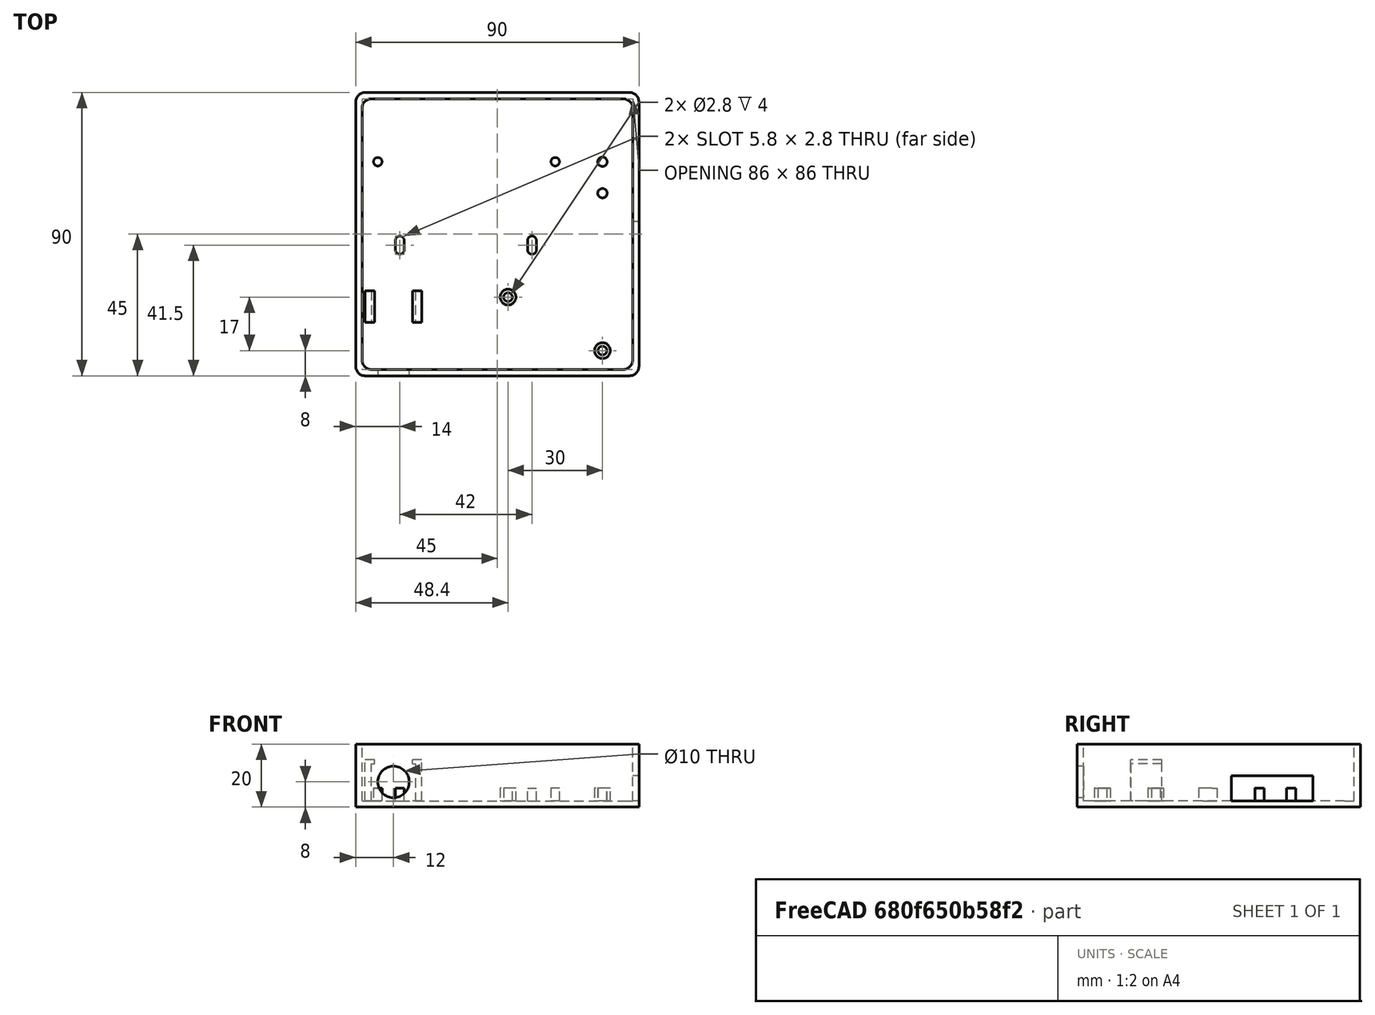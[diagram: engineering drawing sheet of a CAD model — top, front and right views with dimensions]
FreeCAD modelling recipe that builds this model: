
FCSTD DOCUMENT  (FreeCAD 1.0R39109 (Git))
Label: PowerBox
License: All rights reserved
objects: Sketcher::SketchObject×7, PartDesign::Pad×4, PartDesign::Pocket×4, PartDesign::Body×1, Mesh::Feature×1
note: 39 computed .brp shape members not serialized (recipe doc carries the construction recipe); baked Part::Feature solids carry a one-line shape summary decoded from their .brp

FEATURE [Sketcher::SketchObject] Sketch
  ArcFitTolerance = 1e-06
  AttachmentSupport = -> [XY_Plane]
  FullyConstrained = true
  MakeInternals = false
  MapMode = 5
  sketch-geometry (20):
    g0: LineSegment StartX=3 StartY=0 StartZ=0 EndX=87 EndY=0 EndZ=0
    g1: LineSegment StartX=90 StartY=3 StartZ=0 EndX=90 EndY=87 EndZ=0
    g2: LineSegment StartX=87 StartY=90 StartZ=0 EndX=3 EndY=90 EndZ=0
    g3: LineSegment StartX=0 StartY=87 StartZ=0 EndX=0 EndY=3 EndZ=0
    g4: ArcOfCircle CenterX=3 CenterY=3 CenterZ=0 NormalX=0 NormalY=0 NormalZ=1 AngleXU=0 Radius=3 StartAngle=3.14159 EndAngle=4.71239
    g5: ArcOfCircle CenterX=87 CenterY=3 CenterZ=0 NormalX=0 NormalY=0 NormalZ=1 AngleXU=0 Radius=3 StartAngle=4.71239 EndAngle=6.28319
    g6: ArcOfCircle CenterX=87 CenterY=87 CenterZ=0 NormalX=0 NormalY=0 NormalZ=1 AngleXU=0 Radius=3 StartAngle=1.1e-15 EndAngle=1.5708
    g7: ArcOfCircle CenterX=3 CenterY=87 CenterZ=0 NormalX=0 NormalY=0 NormalZ=1 AngleXU=0 Radius=3 StartAngle=1.5708 EndAngle=3.14159
    g8: GeomPoint [constr] X=0 Y=0 Z=0
    g9: GeomPoint [constr] X=90 Y=90 Z=0
    g10: LineSegment StartX=2 StartY=85 StartZ=0 EndX=2 EndY=5 EndZ=0
    g11: LineSegment StartX=5 StartY=2 StartZ=0 EndX=85 EndY=2 EndZ=0
    g12: LineSegment StartX=88 StartY=5 StartZ=0 EndX=88 EndY=85 EndZ=0
    g13: LineSegment StartX=85 StartY=88 StartZ=0 EndX=5 EndY=88 EndZ=0
    g14: ArcOfCircle CenterX=5 CenterY=85 CenterZ=0 NormalX=0 NormalY=0 NormalZ=1 AngleXU=0 Radius=3 StartAngle=1.5708 EndAngle=3.14159
    g15: ArcOfCircle CenterX=5 CenterY=5 CenterZ=0 NormalX=0 NormalY=0 NormalZ=1 AngleXU=0 Radius=3 StartAngle=3.14159 EndAngle=4.71239
    g16: ArcOfCircle CenterX=85 CenterY=5 CenterZ=0 NormalX=0 NormalY=0 NormalZ=1 AngleXU=0 Radius=3 StartAngle=4.71239 EndAngle=6.28319
    g17: ArcOfCircle CenterX=85 CenterY=85 CenterZ=0 NormalX=0 NormalY=0 NormalZ=1 AngleXU=0 Radius=3 StartAngle=1.1e-15 EndAngle=1.5708
    g18: GeomPoint [constr] X=2 Y=88 Z=0
    g19: GeomPoint [constr] X=88 Y=2 Z=0
  constraints (47):
    c: Tangent(g0,g4) = -1.5708
    c: Tangent(g0,g5) = -1.5708
    c: Tangent(g1,g5) = -1.5708
    c: Tangent(g1,g6) = -1.5708
    c: Tangent(g2,g6) = -1.5708
    c: Tangent(g2,g7) = -1.5708
    c: Tangent(g3,g7) = -1.5708
    c: Tangent(g3,g4) = -1.5708
    c: Horizontal(g0)
    c: Horizontal(g2)
    c: Vertical(g1)
    c: Vertical(g3)
    c: Equal(g4,g5)
    c: Equal(g5,g6)
    c: Equal(g6,g7)
    c: PointOnObject(g8,g0)
    c: PointOnObject(g8,g3)
    c: PointOnObject(g9,g1)
    c: PointOnObject(g9,g2)
    c: Distance(g1,g3) = 90
    c: Distance(g0,g2) = 90
    c: Radius(g5) = 3
    c: Coincident(g8,g-1)
    c: Tangent(g10,g14) = -1.5708
    c: Tangent(g10,g15) = -1.5708
    c: Tangent(g11,g15) = -1.5708
    c: Tangent(g11,g16) = -1.5708
    c: Tangent(g12,g16) = -1.5708
    c: Tangent(g12,g17) = -1.5708
    c: Tangent(g13,g17) = -1.5708
    c: Tangent(g13,g14) = -1.5708
    c: Vertical(g10)
    c: Vertical(g12)
    c: Horizontal(g11)
    c: Horizontal(g13)
    c: Equal(g14,g15)
    c: Equal(g15,g16)
    c: Equal(g16,g17)
    c: PointOnObject(g18,g10)
    c: PointOnObject(g18,g13)
    c: PointOnObject(g19,g11)
    c: PointOnObject(g19,g12)
    c: Distance(g10,g12) = 86
    c: Distance(g11,g13) = 86
    c: Radius(g15) = 3
    c: Distance(g0,g11) = 2
    c: Distance(g3,g10) = 2
FEATURE [PartDesign::Pad] Pad
  Direction = (0,0,1)
  Length = 20
  Length2 = 10
  Profile = -> Sketch
  ReferenceAxis = -> Sketch [N_Axis]
  Suppressed = false
  Type = 0
FEATURE [PartDesign::Pad] Pad001
  BaseFeature = -> Pad
  Direction = (0,0,1)
  Length = 2
  Length2 = 10
  Profile = -> Pad [Edge45,Edge42,Edge39,Edge36,Edge33,Edge30,Edge27,Edge47]
  Suppressed = false
  Type = 0
FEATURE [Sketcher::SketchObject] Sketch001
  ArcFitTolerance = 1e-06
  AttachmentSupport = -> [Pad001]
  FullyConstrained = true
  MakeInternals = false
  MapMode = 5
  Placement = pos=(0,0,0) rot=(1,0,0;1.5708rad)
  sketch-geometry (1):
    g0: Circle CenterX=12 CenterY=8 CenterZ=0 NormalX=0 NormalY=0 NormalZ=1 AngleXU=0 Radius=5
  constraints (3):
    c: Diameter(g0) = 10
    c: DistanceY(g-1,g0) = 8
    c: DistanceX(g-1,g0) = 12
FEATURE [PartDesign::Pocket] Pocket
  BaseFeature = -> Pad001
  Direction = (0,1,-2e-16)
  Length = 5
  Length2 = 5
  Profile = -> Sketch001 [Edge1]
  ReferenceAxis = -> Sketch001 [N_Axis]
  Suppressed = false
  Type = 2
FEATURE [Sketcher::SketchObject] Sketch002
  ArcFitTolerance = 1e-06
  AttachmentSupport = -> [Pocket]
  FullyConstrained = true
  MakeInternals = false
  MapMode = 5
  Placement = pos=(0,0,2) rot=(0,0,1;0rad)
  sketch-geometry (8):
    g0: LineSegment StartX=3 StartY=27 StartZ=0 EndX=3 EndY=17 EndZ=0
    g1: LineSegment StartX=3 StartY=17 StartZ=0 EndX=6 EndY=17 EndZ=0
    g2: LineSegment StartX=6 StartY=17 StartZ=0 EndX=6 EndY=27 EndZ=0
    g3: LineSegment StartX=6 StartY=27 StartZ=0 EndX=3 EndY=27 EndZ=0
    g4: LineSegment StartX=18 StartY=27 StartZ=0 EndX=18 EndY=17 EndZ=0
    g5: LineSegment StartX=18 StartY=17 StartZ=0 EndX=21 EndY=17 EndZ=0
    g6: LineSegment StartX=21 StartY=17 StartZ=0 EndX=21 EndY=27 EndZ=0
    g7: LineSegment StartX=21 StartY=27 StartZ=0 EndX=18 EndY=27 EndZ=0
  constraints (24):
    c: Coincident(g0,g1)
    c: Coincident(g1,g2)
    c: Coincident(g2,g3)
    c: Coincident(g3,g0)
    c: Vertical(g0)
    c: Vertical(g2)
    c: Horizontal(g1)
    c: Horizontal(g3)
    c: Coincident(g4,g5)
    c: Coincident(g5,g6)
    c: Coincident(g6,g7)
    c: Coincident(g7,g4)
    c: Vertical(g4)
    c: Vertical(g6)
    c: Horizontal(g5)
    c: Horizontal(g7)
    c: DistanceX(g-1,g0) = 3
    c: DistanceX(g0,g2) = 3
    c: DistanceX(g4,g6) = 3
    c: DistanceX(g2,g4) = 12
    c: DistanceY(g1,g2) = 10
    c: DistanceY(g-1,g0) = 27
    c: Horizontal(g1,g4)
    c: Horizontal(g2,g4)
FEATURE [PartDesign::Pad] Pad002
  BaseFeature = -> Pocket
  Direction = (0,0,1)
  Length = 13
  Length2 = 10
  Profile = -> Sketch002
  ReferenceAxis = -> Sketch002 [N_Axis]
  Suppressed = false
  Type = 0
FEATURE [Sketcher::SketchObject] Sketch003
  ArcFitTolerance = 1e-06
  AttachmentSupport = -> [Pad002]
  ExternalGeometry = -> [Pad002]
  FullyConstrained = true
  MakeInternals = false
  MapMode = 5
  Placement = pos=(0,27,0) rot=(0,0.707107,0.707107;3.14159rad)
  sketch-geometry (4):
    g0: LineSegment StartX=-18 StartY=2 StartZ=0 EndX=-18 EndY=13.8 EndZ=0
    g1: LineSegment StartX=-18 StartY=13.8 StartZ=0 EndX=-19 EndY=13.8 EndZ=0
    g2: LineSegment StartX=-19 StartY=13.8 StartZ=0 EndX=-19 EndY=2 EndZ=0
    g3: LineSegment StartX=-19 StartY=2 StartZ=0 EndX=-18 EndY=2 EndZ=0
  constraints (11):
    c: Coincident(g0,g1)
    c: Coincident(g1,g2)
    c: Coincident(g2,g3)
    c: Coincident(g3,g0)
    c: Vertical(g0)
    c: Vertical(g2)
    c: Horizontal(g1)
    c: Horizontal(g3)
    c: Coincident(g0,g-4)
    c: DistanceY(g2,g2) = 11.8
    c: DistanceX(g1,g1) = 1
FEATURE [PartDesign::Pocket] Pocket001
  BaseFeature = -> Pad002
  Direction = (0,-1,2e-16)
  Length = 5
  Length2 = 5
  Profile = -> Sketch003
  ReferenceAxis = -> Sketch003 [N_Axis]
  Suppressed = false
  Type = 2
FEATURE [Sketcher::SketchObject] Sketch004
  ArcFitTolerance = 1e-06
  AttachmentSupport = -> [Pocket001]
  ExternalGeometry = -> [Pocket001]
  FullyConstrained = true
  MakeInternals = false
  MapMode = 5
  Placement = pos=(0,27,0) rot=(0,0.707107,0.707107;3.14159rad)
  sketch-geometry (4):
    g0: LineSegment StartX=-6 StartY=2 StartZ=0 EndX=-5 EndY=2 EndZ=0
    g1: LineSegment StartX=-5 StartY=2 StartZ=0 EndX=-5 EndY=13.8 EndZ=0
    g2: LineSegment StartX=-5 StartY=13.8 StartZ=0 EndX=-6 EndY=13.8 EndZ=0
    g3: LineSegment StartX=-6 StartY=13.8 StartZ=0 EndX=-6 EndY=2 EndZ=0
  constraints (11):
    c: Coincident(g0,g1)
    c: Coincident(g1,g2)
    c: Coincident(g2,g3)
    c: Coincident(g3,g0)
    c: Horizontal(g0)
    c: Horizontal(g2)
    c: Vertical(g1)
    c: Vertical(g3)
    c: Coincident(g0,g-4)
    c: DistanceY(g0,g2) = 11.8
    c: DistanceX(g2,g2) = 1
FEATURE [PartDesign::Pocket] Pocket002
  BaseFeature = -> Pocket001
  Direction = (0,-1,2e-16)
  Length = 5
  Length2 = 5
  Profile = -> Sketch004
  ReferenceAxis = -> Sketch004 [N_Axis]
  Suppressed = false
  Type = 2
FEATURE [Sketcher::SketchObject] Sketch005
  ArcFitTolerance = 1e-06
  AttachmentSupport = -> [XY_Plane]
  ExternalGeometry = -> [Pocket002]
  FullyConstrained = true
  MakeInternals = false
  MapMode = 5
  sketch-geometry (16):
    g0: Circle CenterX=7 CenterY=68 CenterZ=0 NormalX=0 NormalY=0 NormalZ=1 AngleXU=0 Radius=1.35
    g1: Circle CenterX=63.4 CenterY=68 CenterZ=0 NormalX=0 NormalY=0 NormalZ=1 AngleXU=0 Radius=1.35
    g2: Circle CenterX=78.4 CenterY=68 CenterZ=0 NormalX=0 NormalY=0 NormalZ=1 AngleXU=0 Radius=1.5
    g3: Circle CenterX=78.4 CenterY=58 CenterZ=0 NormalX=0 NormalY=0 NormalZ=1 AngleXU=0 Radius=1.5
    g4: Circle CenterX=78.4 CenterY=8 CenterZ=0 NormalX=0 NormalY=0 NormalZ=1 AngleXU=0 Radius=2.5
    g5: Circle CenterX=48.4 CenterY=25 CenterZ=0 NormalX=0 NormalY=0 NormalZ=1 AngleXU=0 Radius=2.5
    g6: ArcOfCircle CenterX=14 CenterY=43 CenterZ=0 NormalX=0 NormalY=0 NormalZ=1 AngleXU=0 Radius=1.4 StartAngle=-9e-16 EndAngle=3.14159
    g7: ArcOfCircle CenterX=14 CenterY=40 CenterZ=0 NormalX=0 NormalY=0 NormalZ=1 AngleXU=0 Radius=1.4 StartAngle=3.14159 EndAngle=6.28319
    g8: LineSegment StartX=15.4 StartY=43 StartZ=0 EndX=15.4 EndY=40 EndZ=0
    g9: LineSegment StartX=12.6 StartY=43 StartZ=0 EndX=12.6 EndY=40 EndZ=0
    g10: ArcOfCircle CenterX=56 CenterY=43 CenterZ=0 NormalX=0 NormalY=0 NormalZ=1 AngleXU=0 Radius=1.4 StartAngle=7e-16 EndAngle=3.14159
    g11: ArcOfCircle CenterX=56 CenterY=40 CenterZ=0 NormalX=0 NormalY=0 NormalZ=1 AngleXU=0 Radius=1.4 StartAngle=3.14159 EndAngle=6.28319
    g12: LineSegment StartX=57.4 StartY=43 StartZ=0 EndX=57.4 EndY=40 EndZ=0
    g13: LineSegment StartX=54.6 StartY=43 StartZ=0 EndX=54.6 EndY=40 EndZ=0
    g14: Circle CenterX=48.4 CenterY=25 CenterZ=0 NormalX=0 NormalY=0 NormalZ=1 AngleXU=0 Radius=1.4
    g15: Circle CenterX=78.4 CenterY=8 CenterZ=0 NormalX=0 NormalY=0 NormalZ=1 AngleXU=0 Radius=1.4
  constraints (42):
    c: Diameter(g0) = 2.7
    c: Diameter(g1) = 2.7
    c: DistanceX(g-4,g0) = 5
    c: DistanceY(g0,g-3) = 20
    c: Horizontal(g0,g1)
    c: DistanceX(g0,g1) = 56.4
    c: Diameter(g2) = 3
    c: Diameter(g3) = 3
    c: Vertical(g2,g3)
    c: Horizontal(g1,g2)
    c: DistanceX(g1,g2) = 15
    c: DistanceY(g3,g2) = 10
    c: Diameter(g4) = 5
    c: Diameter(g5) = 5
    c: Vertical(g3,g4)
    c: DistanceY(g4,g3) = 50
    c: DistanceY(g4,g5) = 17
    c: DistanceX(g5,g4) = 30
    c: Tangent(g6,g8) = 1.5708
    c: Tangent(g6,g9) = -1.5708
    c: Tangent(g7,g8) = 1.5708
    c: Tangent(g7,g9) = -1.5708
    c: Equal(g6,g7)
    c: Vertical(g9)
    c: Distance(g6,g7) = 3
    c: Radius(g6) = 1.4
    c: Tangent(g10,g12) = 1.5708
    c: Tangent(g10,g13) = -1.5708
    c: Tangent(g11,g12) = 1.5708
    c: Tangent(g11,g13) = -1.5708
    c: Equal(g10,g11)
    c: Vertical(g13)
    c: Distance(g10,g11) = 3
    c: Radius(g10) = 1.4
    c: Horizontal(g7,g11)
    c: DistanceY(g6,g0) = 25
    c: DistanceX(g6,g10) = 42
    c: DistanceX(g0,g6) = 7
    c: Diameter(g14) = 2.8
    c: Coincident(g14,g5)
    c: Diameter(g15) = 2.8
    c: Coincident(g15,g4)
FEATURE [PartDesign::Pad] Pad003
  BaseFeature = -> Pocket002
  Direction = (0,0,1)
  Length = 6
  Length2 = 10
  Profile = -> Sketch005
  ReferenceAxis = -> Sketch005 [N_Axis]
  Suppressed = false
  Type = 0
FEATURE [Sketcher::SketchObject] Sketch006
  ArcFitTolerance = 1e-06
  AttachmentSupport = -> [Pad003]
  ExternalGeometry = -> [Pad003]
  FullyConstrained = true
  MakeInternals = false
  MapMode = 5
  Placement = pos=(90,0,0) rot=(0.57735,0.57735,0.57735;2.0944rad)
  sketch-geometry (4):
    g0: LineSegment StartX=49 StartY=10 StartZ=0 EndX=49 EndY=2 EndZ=0
    g1: LineSegment StartX=49 StartY=2 StartZ=0 EndX=75 EndY=2 EndZ=0
    g2: LineSegment StartX=75 StartY=2 StartZ=0 EndX=75 EndY=10 EndZ=0
    g3: LineSegment StartX=75 StartY=10 StartZ=0 EndX=49 EndY=10 EndZ=0
  constraints (12):
    c: Coincident(g0,g1)
    c: Coincident(g1,g2)
    c: Coincident(g2,g3)
    c: Coincident(g3,g0)
    c: Vertical(g0)
    c: Vertical(g2)
    c: Horizontal(g1)
    c: Horizontal(g3)
    c: Distance(g0,g2) = 26
    c: Distance(g1,g3) = 8
    c: DistanceX(g1,g-4) = 12
    c: DistanceY(g-4,g1) = 2
FEATURE [PartDesign::Pocket] Pocket003
  BaseFeature = -> Pad003
  Direction = (-1,0,0)
  Length = 5
  Length2 = 5
  Profile = -> Sketch006
  ReferenceAxis = -> Sketch006 [N_Axis]
  Suppressed = false
  Type = 2
FEATURE [PartDesign::Body] Body
  AllowCompound = false
  Group = -> [Sketch,Pad,Pad001,Sketch001,Pocket,Sketch002,Pad002,Sketch003,Pocket001,Sketch004,Pocket002,Sketch005,Pad003,Sketch006,Pocket003]
  Origin = -> Origin
  Tip = -> Pocket003
FEATURE [Mesh::Feature] Mesh  label="Pocket003 (Meshed)"
